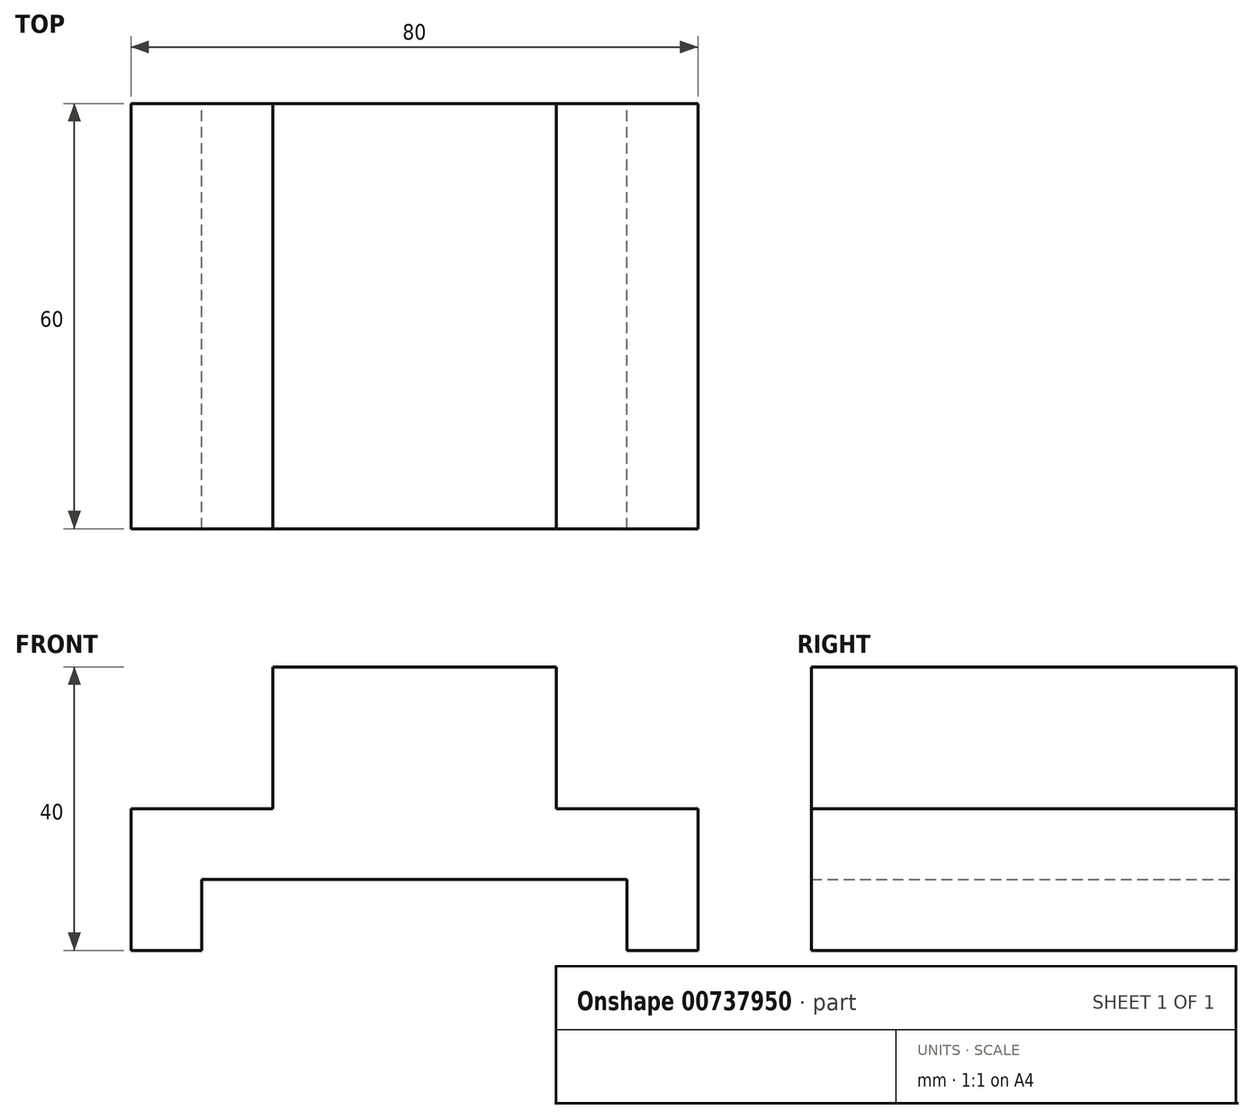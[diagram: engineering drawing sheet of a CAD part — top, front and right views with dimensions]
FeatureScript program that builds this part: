
annotation { "Feature Type Name" : "Feature", "Feature Type Description" : "" }
export const myFeature = defineFeature(function(context is Context, id is Id, definition is map)
    precondition{}
    {
        {
            var Q0;
            Q0=qCreatedBy(makeId("Front.planeOp"),FACE);
            var sketch = newSketch(context, id + "F0", { "sketchPlane" : qUnion([Q0])});
            skLineSegment(sketch, "E0", {"start": v(-10, 0) * mm, "end": v(-10, 20) * mm});
            skLineSegment(sketch, "E1", {"start": v(-10, 20) * mm, "end": v(10, 20) * mm});
            skLineSegment(sketch, "E2", {"start": v(10, 20) * mm, "end": v(10, 40) * mm});
            skLineSegment(sketch, "E3", {"start": v(10, 40) * mm, "end": v(50, 40) * mm});
            skLineSegment(sketch, "E4", {"start": v(50, 40) * mm, "end": v(50, 20) * mm});
            skLineSegment(sketch, "E5", {"start": v(50, 20) * mm, "end": v(70, 20) * mm});
            skLineSegment(sketch, "E6", {"start": v(70, 20) * mm, "end": v(70, 0) * mm});
            skLineSegment(sketch, "E7", {"start": v(70, 0) * mm, "end": v(60, 0) * mm});
            skLineSegment(sketch, "E8", {"start": v(60, 0) * mm, "end": v(60, 10) * mm});
            skLineSegment(sketch, "E9", {"start": v(60, 10) * mm, "end": v(0, 10) * mm});
            skLineSegment(sketch, "E10", {"start": v(0, 10) * mm, "end": v(0, 0) * mm});
            skLineSegment(sketch, "E11", {"start": v(0, 0) * mm, "end": v(-10, 0) * mm});
            skSolve(sketch);
        }
        {
            var Q0;
            Q0=makeQuery(id+"F0.imprint","IMPRINT",FACE,{"disambiguationData":[TD([[makeQuery(id+"F0.imprint","IMPRINT",EDGE,{"derivedFrom":sQuery(id+"F0.wireOp",EDGE,"E0")}),-1.0]])]});
            extrude(context, id + "F1", {"entities" : qUnion([Q0]), "depth" : 60 * mm, "offsetDistance" : 25 * mm});
        }
    });
